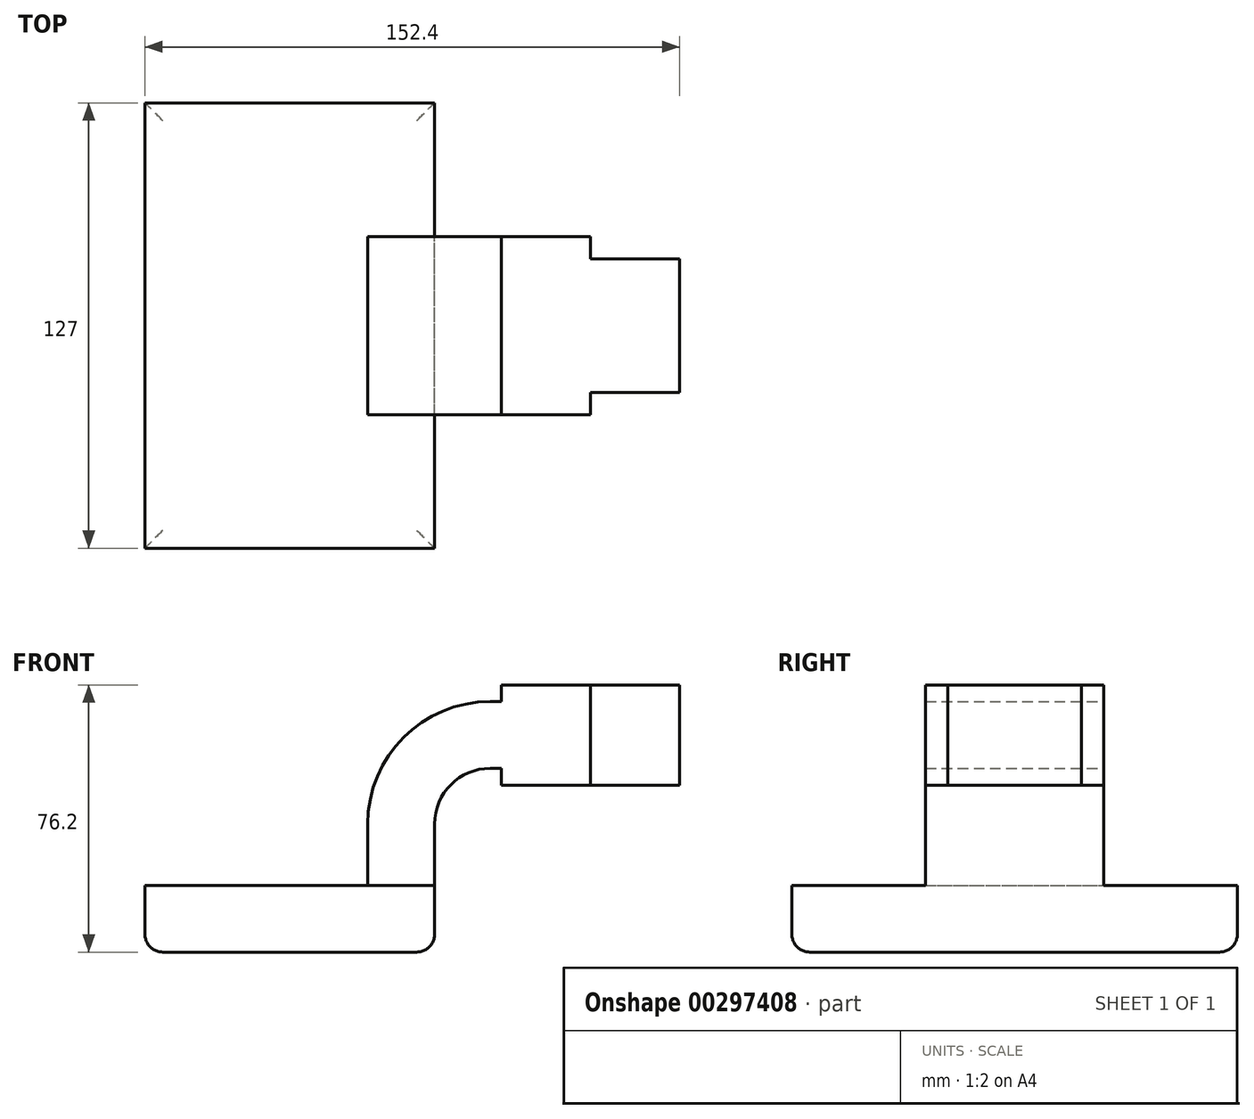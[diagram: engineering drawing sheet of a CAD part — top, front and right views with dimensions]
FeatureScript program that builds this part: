
annotation { "Feature Type Name" : "Feature", "Feature Type Description" : "" }
export const myFeature = defineFeature(function(context is Context, id is Id, definition is map)
    precondition{}
    {
        {
            var Q0;
            Q0=qCreatedBy(makeId("Front.planeOp"),FACE);
            var sketch = newSketch(context, id + "F0", { "sketchPlane" : qUnion([Q0])});
            skLineSegment(sketch, "E0.bottom", {"start": v(41.28, -9.52) * mm, "end": v(-41.28, -9.53) * mm});
            skLineSegment(sketch, "E0.top", {"start": v(41.28, 9.53) * mm, "end": v(-41.28, 9.52) * mm});
            skLineSegment(sketch, "E0.left", {"start": v(41.28, -9.52) * mm, "end": v(41.28, 9.53) * mm});
            skLineSegment(sketch, "E0.right", {"start": v(-41.28, -9.53) * mm, "end": v(-41.28, 9.52) * mm});
            skPoint(sketch, "E0.middle", {"position": v(0, 0) * mm});
            skLineSegment(sketch, "E1.bottom", {"start": v(60.33, 38.1) * mm, "end": v(111.12, 38.1) * mm});
            skLineSegment(sketch, "E1.top", {"start": v(60.32, 66.68) * mm, "end": v(111.12, 66.68) * mm});
            skLineSegment(sketch, "E1.left", {"start": v(60.33, 38.1) * mm, "end": v(60.33, 66.68) * mm});
            skLineSegment(sketch, "E1.right", {"start": v(111.12, 38.1) * mm, "end": v(111.12, 66.68) * mm});
            skPoint(sketch, "E1.middle", {"position": v(85.72, 52.39) * mm});
            skLineSegment(sketch, "E2", {"start": v(41.28, 9.53) * mm, "end": v(41.28, 27) * mm});
            skArc(sketch, "E3", {"start": v(41.28, 27) * mm, "mid": v(45.92, 38.23) * mm, "end": v(57.15, 42.88) * mm});
            skLineSegment(sketch, "E4", {"start": v(57.15, 42.88) * mm, "end": v(85.72, 42.88) * mm});
            skLineSegment(sketch, "E5.0", {"start": v(57.15, 61.93) * mm, "end": v(85.72, 61.93) * mm});
            skArc(sketch, "E5.1", {"start": v(22.23, 27) * mm, "mid": v(32.45, 51.7) * mm, "end": v(57.15, 61.93) * mm});
            skLineSegment(sketch, "E5.2", {"start": v(22.23, 9.53) * mm, "end": v(22.23, 27) * mm});
            skLineSegment(sketch, "E6", {"start": v(85.72, 38.1) * mm, "end": v(85.72, 66.68) * mm});
            skFitSpline(sketch, "E7", {"points": [v(-41.28, 9.52) * mm, v(57.15, 61.93) * mm], "startDerivative": vector(-14.91, 165.81) * mm, "endDerivative": vector(93.87, -2.6) * mm});
            skSolve(sketch);
        }
        {
            var Q0;
            Q0=makeQuery(id+"F0.imprint","IMPRINT",FACE,{"disambiguationData":[TD([[makeQuery(id+"F0.imprint","IMPRINT",EDGE,{"derivedFrom":sQuery(id+"F0.wireOp",EDGE,"E0.bottom")}),-1.0]])]});
            extrude(context, id + "F1", {"entities" : qUnion([Q0]), "endBound" : BoundingType.SYMMETRIC, "depth" : 127 * mm});
        }
        {
            var Q0;
            {var subQ1=sQuery(id+"F0.wireOp",EDGE,"E2");Q0=makeQuery(id+"F0.imprint","IMPRINT",FACE,{"disambiguationData":[TD([[makeQuery(id+"F0.imprint","IMPRINT",EDGE,{"derivedFrom":subQ1}),1.0]])]});}
            var Q1;
            {var subQ0=sQuery(id+"F0.wireOp",EDGE,"E4");var subQ1=sQuery(id+"F0.wireOp",EDGE,"E1.left");var subQ2=makeQuery(id+"F0.imprint","INTERSECT",VERTEX,{"derivedFrom":[subQ1,subQ0]});Q1=makeQuery(id+"F0.imprint","IMPRINT",FACE,{"disambiguationData":[TD([[makeQuery(id+"F0.imprint","IMPRINT",EDGE,{"disambiguationData":[TD([[subQ2,-1.0]])],"derivedFrom":subQ1}),-1.0]])]});}
            var Q2;
            {var subQ0=sQuery(id+"F0.wireOp",EDGE,"E1.left");var subQ1=sQuery(id+"F0.wireOp",EDGE,"E1.top");var subQ2=makeQuery(id+"F0.imprint","INTERSECT",VERTEX,{"derivedFrom":[subQ1,subQ0]});Q2=makeQuery(id+"F0.imprint","IMPRINT",FACE,{"disambiguationData":[TD([[makeQuery(id+"F0.imprint","IMPRINT",EDGE,{"disambiguationData":[TD([[subQ2,-1.0]])],"derivedFrom":subQ1}),-1.0]])]});}
            var Q3;
            {var subQ0=sQuery(id+"F0.wireOp",EDGE,"E1.left");var subQ1=sQuery(id+"F0.wireOp",EDGE,"E1.bottom");var subQ2=makeQuery(id+"F0.imprint","INTERSECT",VERTEX,{"derivedFrom":[subQ1,subQ0]});Q3=makeQuery(id+"F0.imprint","IMPRINT",FACE,{"disambiguationData":[TD([[makeQuery(id+"F0.imprint","IMPRINT",EDGE,{"disambiguationData":[TD([[subQ2,-1.0]])],"derivedFrom":subQ1}),1.0]])]});}
            extrude(context, id + "F2", {"entities" : qUnion([Q0, Q1, Q2, Q3]), "operationType" : NewBodyOperationType.ADD, "endBound" : BoundingType.SYMMETRIC, "depth" : 50.8 * mm});
        }
        {
            var Q0;
            Q0=makeQuery(id+"F0.imprint","IMPRINT",FACE,{"disambiguationData":[TD([[makeQuery(id+"F0.imprint","IMPRINT",EDGE,{"derivedFrom":sQuery(id+"F0.wireOp",EDGE,"E5.1")}),1.0]])]});
            extrude(context, id + "F3", {"entities" : qUnion([Q0]), "operationType" : NewBodyOperationType.ADD, "endBound" : BoundingType.SYMMETRIC, "depth" : 6.35 * mm});
        }
        {
            var Q0;
            Q0=makeQuery(id+"F1.opExtrude","CAP_EDGE",EDGE,{"disambiguationData":[OSD([sQuery(id+"F0.wireOp",EDGE,"E0.bottom")])],"isStart":false});
            var Q1;
            Q1=makeQuery(id+"F1.opExtrude","SWEPT_EDGE",EDGE,{"disambiguationData":[OSD([sQuery(id+"F0.wireOp",EDGE,"E0.bottom"),sQuery(id+"F0.wireOp",EDGE,"E0.left")])]});
            var Q2;
            Q2=makeQuery(id+"F1.opExtrude","CAP_EDGE",EDGE,{"disambiguationData":[OSD([sQuery(id+"F0.wireOp",EDGE,"E0.bottom")])],"isStart":true});
            var Q3;
            Q3=makeQuery(id+"F1.opExtrude","SWEPT_EDGE",EDGE,{"disambiguationData":[OSD([sQuery(id+"F0.wireOp",EDGE,"E0.bottom"),sQuery(id+"F0.wireOp",EDGE,"E0.right")])]});
            fillet(context, id + "F4", {"entities" : qUnion([Q0, Q1, Q2, Q3]), "radius" : 5.08 * mm, "tangentPropagation" : true, "allowEdgeOverflow" : false});
        }
        {
            var Q0;
            {var subQ0=sQuery(id+"F0.wireOp",EDGE,"E1.right");Q0=makeQuery(id+"F0.imprint","IMPRINT",FACE,{"disambiguationData":[TD([[makeQuery(id+"F0.imprint","IMPRINT",EDGE,{"derivedFrom":subQ0}),1.0]])]});}
            extrude(context, id + "F5", {"entities" : qUnion([Q0]), "operationType" : NewBodyOperationType.ADD, "endBound" : BoundingType.SYMMETRIC, "depth" : 38.1 * mm});
        }
    });
